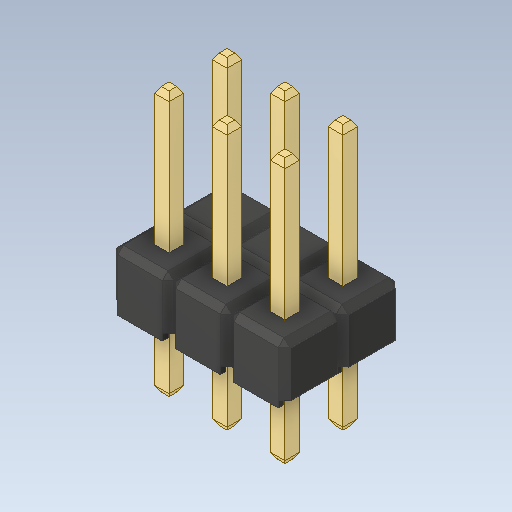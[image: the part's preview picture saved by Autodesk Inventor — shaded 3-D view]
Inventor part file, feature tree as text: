
AUTODESK INVENTOR PART (.ipt)
format: ipt  version: 2020 (Build 240168000, 168)  size: 271,360 bytes
history: native  units: in
note: dims shown in document units (in); Inventor stores cm internally (conversion verified against a paired STEP export)
features: other x11, chamfer x1
ambient origin geometry x8: Origin, YZ Plane, XZ Plane, XY Plane, X Axis, Y Axis, Z Axis, Center Point
bodies: Solid1 (feature_tree), Solid2 (feature_tree), Solid3 (feature_tree), Solid4 (feature_tree), Solid5 (feature_tree), Solid6 (feature_tree), Solid7 (feature_tree), Solid8 (feature_tree), Solid9 (feature_tree), Solid10 (feature_tree), Solid11 (feature_tree), Solid12 (feature_tree)
feature tree (12):
  chamfer  "Chamfer2"  [1 undecoded]
  other  "Boss-Extrude3"
  other  "LPattern1[1]"
  other  "LPattern1[2]"
  other  "LPattern1[3]"
  other  "LPattern1[4]"
  other  "LPattern1[5]"
  other  "LPattern1[6]"
  other  "LPattern1[7]"
  other  "LPattern1[8]"
  other  "LPattern1[9]"
  other  "LPattern1[10]"
note: 1 required parameter value undecoded (feature->parameter linkage not recoverable at this tier; creation-order binding heuristic only, values carry confidence <= 0.55)
